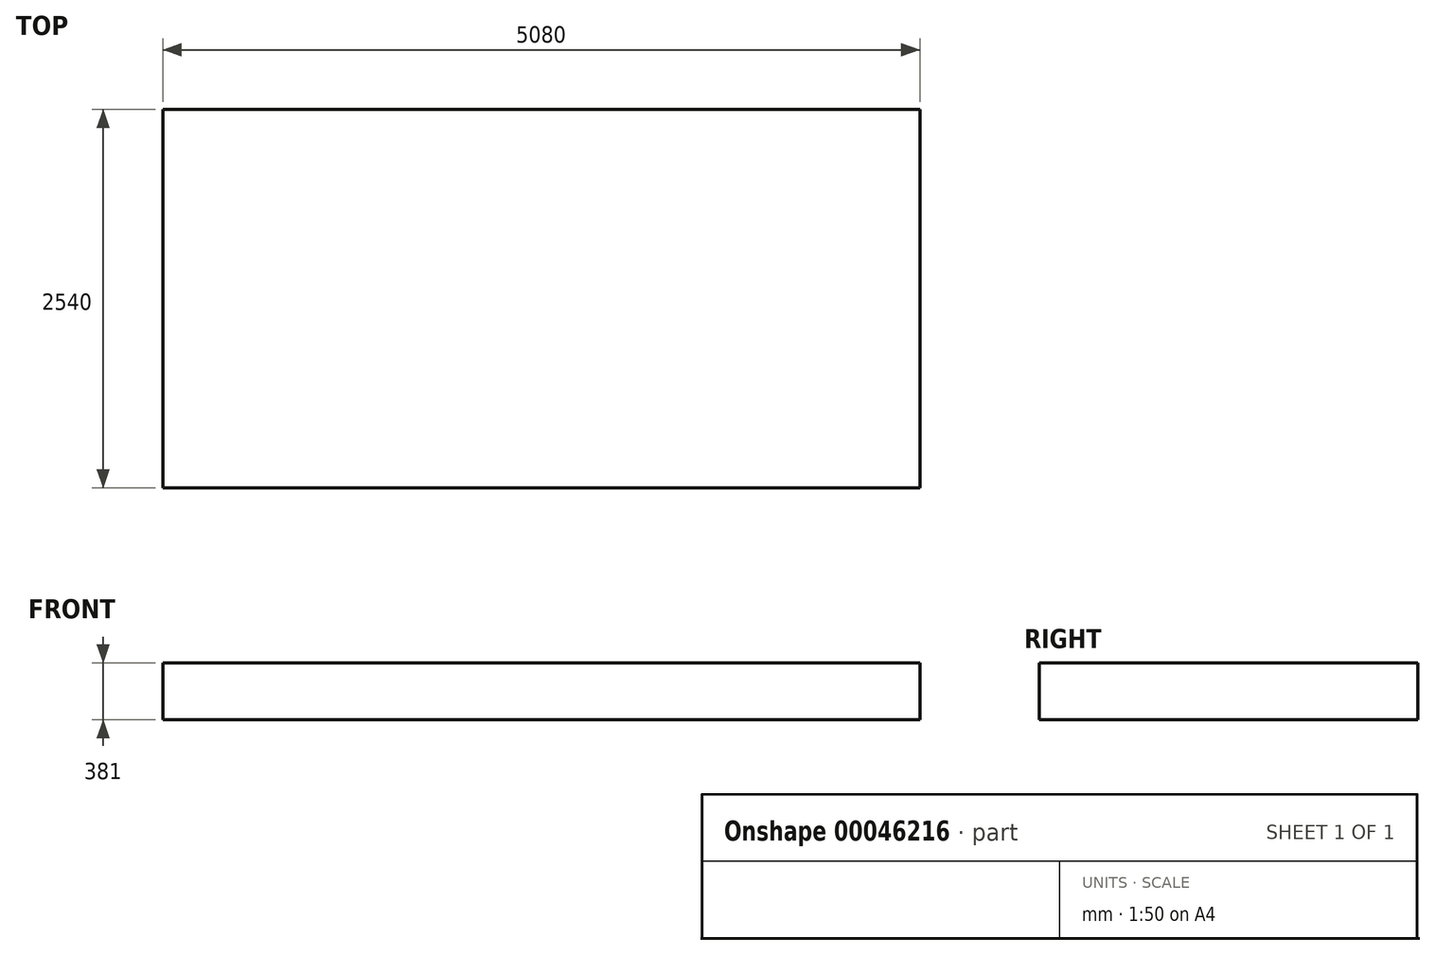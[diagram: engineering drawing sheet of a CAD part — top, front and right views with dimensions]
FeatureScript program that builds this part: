
annotation { "Feature Type Name" : "Feature", "Feature Type Description" : "" }
export const myFeature = defineFeature(function(context is Context, id is Id, definition is map)
    precondition{}
    {
        {
            var Q0;
            Q0=qCreatedBy(makeId("Top.planeOp"),FACE);
            var sketch = newSketch(context, id + "F0", { "sketchPlane" : qUnion([Q0])});
            skLineSegment(sketch, "E0.rect.bottom", {"start": v(2540, 1270) * mm, "end": v(-2540, 1270) * mm});
            skLineSegment(sketch, "E0.rect.top", {"start": v(2540, -1270) * mm, "end": v(-2540, -1270) * mm});
            skLineSegment(sketch, "E0.rect.left", {"start": v(2540, 1270) * mm, "end": v(2540, -1270) * mm});
            skLineSegment(sketch, "E0.rect.right", {"start": v(-2540, 1270) * mm, "end": v(-2540, -1270) * mm});
            skPoint(sketch, "E0.rect.middle", {"position": v(0, 0) * mm});
            skSolve(sketch);
        }
        {
            var Q0;
            Q0=makeQuery(id+"F0.imprint","IMPRINT",FACE,{"disambiguationData":[TD([[makeQuery(id+"F0.imprint","IMPRINT",EDGE,{"derivedFrom":sQuery(id+"F0.wireOp",EDGE,"E0.rect.bottom")}),1.0]])]});
            extrude(context, id + "F1", {"entities" : qUnion([Q0]), "depth" : 381 * mm});
        }
    });
